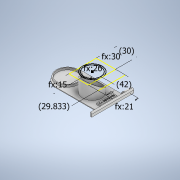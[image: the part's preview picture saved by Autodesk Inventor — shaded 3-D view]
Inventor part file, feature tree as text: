
AUTODESK INVENTOR PART (.ipt)
format: ipt  version: 2021 (Build 250183000, 183)  size: 1,009,152 bytes
history: native  units: in
note: dims shown in document units (in); Inventor stores cm internally (conversion verified against a paired STEP export)
features: extrude x10, sketch x9, fillet x3, chamfer x1
ambient origin geometry x8: Origin, YZ Plane, XZ Plane, XY Plane, X Axis, Y Axis, Z Axis, Center Point
bodies: Solid1 (feature_tree)
feature tree (23):
  extrude  "Extrusion1"  Depth=1.6535in
  extrude  "Extrusion2"  Depth=1.6535in
  sketch  "Sketch5"  dims[d5=1.1811in d6=0.0in d7=1.1024in d8=0.0in]
  extrude  "Extrusion3"  TaperAngle=0.0deg  [1 undecoded]
  chamfer  "Chamfer3"  Distance=1.1024in
  extrude  "Extrusion4"  Depth=0.5906in
  extrude  "Extrusion5"  Depth=1.1811in
  fillet  "Fillet3"  Radius=1.6535in
  extrude  "Extrusion8"  Depth=1.6535in
  extrude  "Extrusion9"  Depth=1.1811in
  extrude  "Extrusion10"  Depth=1.2402in
  fillet  "Fillet4"  Radius=0.8268in
  fillet  "Fillet5"  Radius=1.3386in
  extrude  "Extrusion11"  Depth=0.8268in
  extrude  "Extrusion12"  Depth=0.0394in
  sketch  "Sketch1"  dims[d0=3.3465in d1=1.6535in]
  sketch  "Sketch2"  dims[d2=0.0394in d3=0.0in d4=1.6535in]
  sketch  "Sketch6"  dims[d20=1.0236in d21=0.5906in]
  sketch  "Sketch9"  dims[d22=0.8268in d23=1.1811in d24=1.6535in]
  sketch  "Sketch10"  dims[d25=1.1024in d26=0.0in d30=1.6535in]
  sketch  "Sketch11"  dims[d31=1.1024in d32=45.0deg d34=1.1811in]
  sketch  "Sketch12"  dims[d35=1.1024in d36=0.0in d37=1.2402in d38=0.8268in d39=1.3386in]
  sketch  "Sketch13"  dims[d40=0.1181in d41=0.0in d42=0.8268in d49=0.0394in d50=2.5591in d51=0.0787in d52=0.0in d53=0.4528in d54=0.1969in d55=0.0in d56=0.4528in d58=0.0in d59=0.2362in d60=0.0in d61=0.2323in d62=0.0787in d63=1.1745in d64=0.6693in d65=0.2362in d66=0.315in d67=0.315in d68=0.1772in d69=0.1772in d70=0.0787in d71=0.0in d72=0.0in d73=0.0in d74=0.0in d75=0.0in d76=0.0787in d77=0.0in d79=0.0197in d80=0.0344in d81=0.0197in d82=0.0344in]
note: 1 required parameter value undecoded (feature->parameter linkage not recoverable at this tier; creation-order binding heuristic only, values carry confidence <= 0.55)
